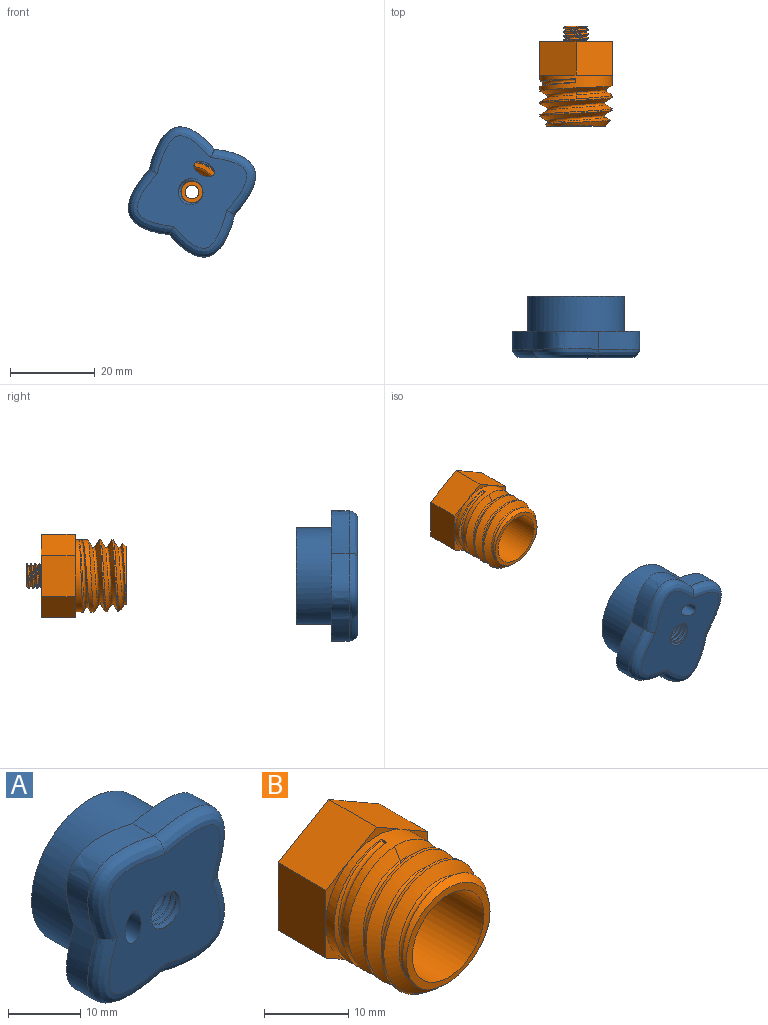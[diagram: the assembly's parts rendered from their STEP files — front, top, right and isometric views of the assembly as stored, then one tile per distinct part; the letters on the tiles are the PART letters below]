
ASSEMBLY  parts=2 mates=1
PART A: 26 faces, bbox 32.5x17.2x31.1 mm
  f0: plane 23.78x23.78mm, normal (0,1,0), area 207.4mm2, adj f15,f21,f22,f23,f24
  f1: plane 16.9x16.86mm, normal (0,1,0), area 166.5mm2, adj f16,f17,f18,f19,f20,f21,f22,f23
  f2: plane 15.79x15.13mm, normal (0,1,0), area 44.5mm2, adj f7,f15
  f3: plane 15.79x15.13mm, normal (0,1,0), area 44.5mm2, adj f8,f15
  f4: plane 15.79x15.13mm, normal (0,1,0), area 44.5mm2, adj f5,f15
  f5: extruded ~12.93x12.3mm, area 96.5mm2, adj f4,f6,f8,f14
  f6: extruded ~12.93x12.3mm, area 96.5mm2, adj f5,f7,f10,f12
  f7: extruded ~12.93x12.3mm, area 96.5mm2, adj f2,f6,f8,f11
  f8: extruded ~12.93x12.3mm, area 96.5mm2, adj f3,f5,f7,f13
  f9: plane 22.01x20.75mm, normal (0,-1,0), area 371mm2, adj f11,f12,f13,f14,f16,f17,f18,f19
  f10: plane 15.79x15.13mm, normal (0,1,0), area 44.5mm2, adj f6,f15
  f11: bspline ~14.61x13.3mm, area 72.5mm2, adj f7,f9,f12,f13
  f12: bspline ~15.48x15.16mm, area 72.5mm2, adj f6,f9,f11,f14
  f13: bspline ~15.48x15.16mm, area 72.5mm2, adj f8,f9,f11,f14
  f14: bspline ~14.61x13.3mm, area 72.5mm2, adj f5,f9,f12,f13
  f15: cylinder r=11.44mm len=22.88mm, axis (0,-1,0), area 598mm2, adj f0,f2,f3,f4,f10
  f16: bspline ~7.3x6.91mm, area 70.7mm2, adj f1,f9,f18,f19
  f17: bspline ~7.3x7.09mm, area 70.7mm2, adj f1,f9,f18,f19
  f18: bspline ~7.41x6.72mm, area 18.1mm2, adj f1,f9,f16,f17
  f19: cylinder r=2.6mm len=6.24mm, axis (0,-1,0), area 26.5mm2, adj f1,f9,f16,f17
  f20: extruded ~6.24x5.2mm, area 82.8mm2, adj f1,f9,f25
  f21: bspline ~20.71x17.94mm, area 265.8mm2, adj f0,f1,f23,f24
  f22: bspline ~20.71x17.94mm, area 265.8mm2, adj f0,f1,f23,f24,f25
  f23: bspline ~21.04x18.22mm, area 68.4mm2, adj f0,f1,f21,f22
  f24: cylinder r=7.28mm len=14.56mm, axis (0,1,0), area 95.3mm2, adj f0,f1,f21,f22,f25
  f25: plane 4.02x0.78mm, normal (0,-1,0), area 1.1mm2, adj f20,f22,f24
PART B: 35 faces, bbox 19.9x25.5x20.1 mm
  f0: cylinder r=8.5mm len=17mm, axis (0,1,0), area 146.4mm2, adj f2,f4,f5,f6,f7,f8,f18,f26
  f1: cylinder r=8.5mm len=16.35mm, axis (0,1,0), area 7.5mm2, adj f2,f30,f31,f33
  f2: cylinder r=8.5mm len=17mm, axis (0,1,0), area 20mm2, adj f0,f1,f30,f31
  f3: plane 6x6mm, normal (0,-1,0), area 20.2mm2, adj f17,f34
  f4: plane 7.36x4.25mm, normal (0,-1,0), area 3.9mm2, adj f0,f11,f12
  f5: plane 7.36x4.25mm, normal (0,-1,0), area 3.9mm2, adj f0,f11,f16
  f6: plane 8.5x2.45mm, normal (0,-1,0), area 3.9mm2, adj f0,f15,f16
  f7: plane 7.36x4.25mm, normal (0,-1,0), area 3.9mm2, adj f0,f14,f15
  f8: plane 7.36x4.25mm, normal (0,-1,0), area 3.9mm2, adj f0,f13,f14
  f9: plane 5.04x4.97mm, normal (0,1,0), area 11.3mm2, adj f17,f20,f21,f22,f23
  f10: cylinder r=3mm len=6mm, axis (0,-1,0), area 7.7mm2, adj f19,f21,f22,f23
  f11: plane 9.82x8mm, normal (-1,0,0), area 78.5mm2, adj f4,f5,f12,f16,f19
  f12: plane 8.5x8mm, normal (-0.5,0,-0.87), area 78.5mm2, adj f4,f11,f13,f18,f19
  f13: plane 8.5x8mm, normal (0.5,0,-0.87), area 78.5mm2, adj f8,f12,f14,f18,f19
  f14: plane 9.82x8mm, normal (1,0,0), area 78.5mm2, adj f7,f8,f13,f15,f19
  f15: plane 8.5x8mm, normal (0.5,0,0.87), area 78.5mm2, adj f6,f7,f14,f16,f19
  f16: plane 8.5x8mm, normal (-0.5,0,0.87), area 78.5mm2, adj f5,f6,f11,f15,f19
  f17: cylinder r=1.6mm len=11.6mm, axis (0,1,0), area 116.6mm2, adj f3,f9
  f18: plane 8.5x2.45mm, normal (0,-1,0), area 3.9mm2, adj f0,f12,f13
  f19: plane 19.91x17.28mm, normal (0,1,0), area 227.5mm2, adj f10,f11,f12,f13,f14,f15,f16,f20
  f20: bspline ~5.68x4.92mm, area 15.4mm2, adj f9,f19,f21,f22
  f21: bspline ~6.93x6mm, area 37.4mm2, adj f9,f10,f19,f20,f23
  f22: bspline ~6.93x6mm, area 37.4mm2, adj f9,f10,f19,f20,f23
  f23: cone r=3mm half-angle=63.4deg, axis (0,-1,0), area 3.9mm2, adj f9,f10,f21,f22
  f24: cylinder r=6mm len=12mm, axis (0,1,0), area 339.3mm2, adj f25,f34
  f25: plane 14.09x13.84mm, normal (0,-1,0), area 38.1mm2, adj f24,f29,f30,f31,f33
  f26: plane 0.91x0.31mm, normal (-1,0.01,0), area 0.2mm2, adj f0,f27,f28,f32
  f27: bspline ~19.31x18.63mm, area 50.6mm2, adj f0,f26,f30,f32
  f28: bspline ~19.32x18.63mm, area 50.5mm2, adj f0,f26,f31,f32
  f29: bspline ~15.88x13.75mm, area 91.7mm2, adj f25,f30,f31,f32
  f30: bspline ~19.63x17mm, area 176.5mm2, adj f1,f2,f25,f27,f29,f33
  f31: bspline ~19.63x17mm, area 228.5mm2, adj f0,f1,f2,f25,f28,f29,f33
  f32: bspline ~16.06x15.36mm, area 39.7mm2, adj f26,f27,f28,f29
  f33: cone r=8.5mm half-angle=36.1deg, axis (0,1,0), area 50.1mm2, adj f1,f25,f30,f31
  f34: torus R=3mm, axis (0,-1,0), area 145.4mm2, adj f3,f24
PLACE A rot(axis=(0,1,0),118deg) t=(7.39,-101.34,32.89)mm
PLACE B t=(7.3,-32.64,32.94)mm fixed
MATE cylindrical B.f24 <-> A.f19  axis (0,-1,0) through (7.3,-52.64,32.94)mm
